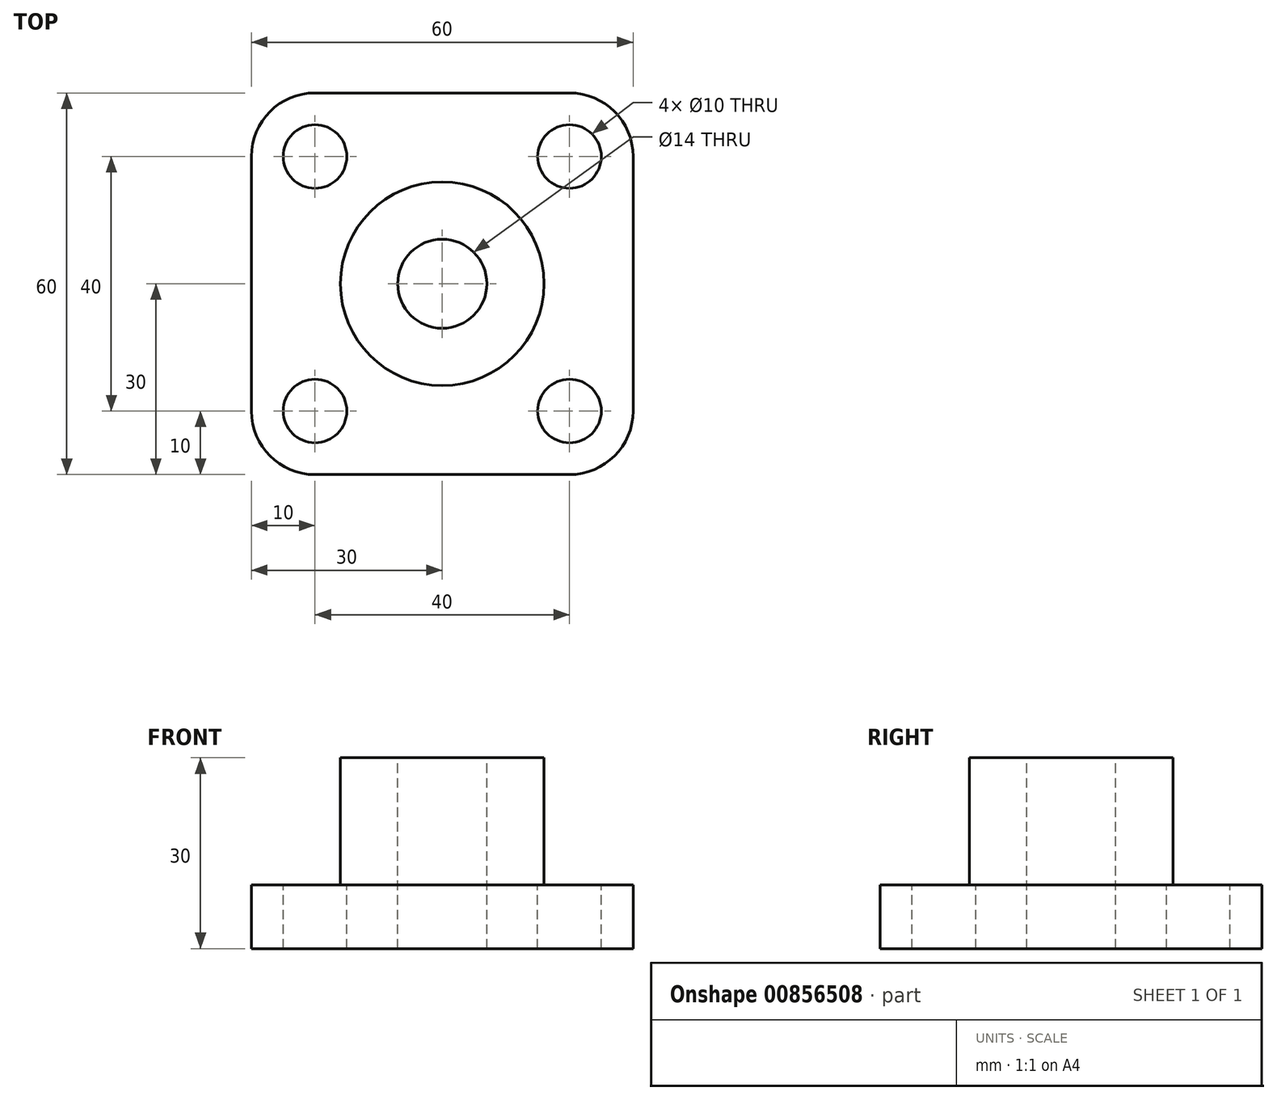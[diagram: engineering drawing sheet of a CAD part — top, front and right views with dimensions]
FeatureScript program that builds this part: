
annotation { "Feature Type Name" : "Feature", "Feature Type Description" : "" }
export const myFeature = defineFeature(function(context is Context, id is Id, definition is map)
    precondition{}
    {
        {
            var Q0;
            Q0=qCreatedBy(makeId("Top.planeOp"),FACE);
            var sketch = newSketch(context, id + "F0", { "sketchPlane" : qUnion([Q0])});
            skLineSegment(sketch, "E0.bottom", {"start": v(30, 30) * mm, "end": v(-30, 30) * mm});
            skLineSegment(sketch, "E0.top", {"start": v(30, -30) * mm, "end": v(-30, -30) * mm});
            skLineSegment(sketch, "E0.left", {"start": v(30, 30) * mm, "end": v(30, -30) * mm});
            skLineSegment(sketch, "E0.right", {"start": v(-30, 30) * mm, "end": v(-30, -30) * mm});
            skPoint(sketch, "E0.middle", {"position": v(0, 0) * mm});
            skSolve(sketch);
        }
        {
            var Q0;
            Q0=makeQuery(id+"F0.imprint","IMPRINT",FACE,{"disambiguationData":[TD([[makeQuery(id+"F0.imprint","IMPRINT",EDGE,{"derivedFrom":sQuery(id+"F0.wireOp",EDGE,"E0.bottom")}),1.0]])]});
            extrude(context, id + "F1", {"entities" : qUnion([Q0]), "depth" : 10 * mm, "offsetDistance" : 25 * mm});
        }
        {
            var Q0;
            Q0=makeQuery(id+"F1.opExtrude","SWEPT_EDGE",EDGE,{"disambiguationData":[OSD([sQuery(id+"F0.wireOp",EDGE,"E0.bottom"),sQuery(id+"F0.wireOp",EDGE,"E0.right")])]});
            var Q1;
            Q1=makeQuery(id+"F1.opExtrude","SWEPT_EDGE",EDGE,{"disambiguationData":[OSD([sQuery(id+"F0.wireOp",EDGE,"E0.top"),sQuery(id+"F0.wireOp",EDGE,"E0.right")])]});
            var Q2;
            Q2=makeQuery(id+"F1.opExtrude","SWEPT_EDGE",EDGE,{"disambiguationData":[OSD([sQuery(id+"F0.wireOp",EDGE,"E0.top"),sQuery(id+"F0.wireOp",EDGE,"E0.left")])]});
            var Q3;
            Q3=makeQuery(id+"F1.opExtrude","SWEPT_EDGE",EDGE,{"disambiguationData":[OSD([sQuery(id+"F0.wireOp",EDGE,"E0.bottom"),sQuery(id+"F0.wireOp",EDGE,"E0.left")])]});
            fillet(context, id + "F2", {"entities" : qUnion([Q0, Q1, Q2, Q3]), "radius" : 10 * mm, "tangentPropagation" : true, "allowEdgeOverflow" : false});
        }
        {
            var Q0;
            Q0=makeQuery(id+"F1.opExtrude","CAP_FACE",FACE,{"disambiguationData":[OSD([sQuery(id+"F0.wireOp",EDGE,"E0.bottom"),sQuery(id+"F0.wireOp",EDGE,"E0.top"),sQuery(id+"F0.wireOp",EDGE,"E0.left"),sQuery(id+"F0.wireOp",EDGE,"E0.right")])],"isStart":false});
            var sketch = newSketch(context, id + "F3", { "sketchPlane" : qUnion([Q0])});
            skCircle(sketch, "E1", {"center": v(0, 0) * mm, "radius": 16 * mm});
            skLineSegment(sketch, "E2", {"start": v(30, 0) * mm, "end": v(30, 3) * mm});
            skLineSegment(sketch, "E3", {"start": v(30, 3) * mm, "end": v(15.72, 3) * mm});
            skLineSegment(sketch, "E4", {"start": v(30, 0) * mm, "end": v(30, -3) * mm});
            skLineSegment(sketch, "E5", {"start": v(30, -3) * mm, "end": v(15.72, -3) * mm});
            skLineSegment(sketch, "E6", {"start": v(0, 30) * mm, "end": v(3, 30) * mm});
            skLineSegment(sketch, "E7", {"start": v(3, 30) * mm, "end": v(3, 15.72) * mm});
            skLineSegment(sketch, "E8", {"start": v(0, 30) * mm, "end": v(-3, 30) * mm});
            skLineSegment(sketch, "E9", {"start": v(-3, 30) * mm, "end": v(-3, 15.72) * mm});
            skLineSegment(sketch, "E10", {"start": v(-30, 0) * mm, "end": v(-30, 3) * mm});
            skLineSegment(sketch, "E11", {"start": v(-30, 3) * mm, "end": v(-15.72, 3) * mm});
            skLineSegment(sketch, "E12", {"start": v(-30, 0) * mm, "end": v(-30, -3) * mm});
            skLineSegment(sketch, "E13", {"start": v(-30, -3) * mm, "end": v(-15.72, -3) * mm});
            skLineSegment(sketch, "E14", {"start": v(0, -30) * mm, "end": v(3, -30) * mm});
            skLineSegment(sketch, "E15", {"start": v(3, -30) * mm, "end": v(3, -15.72) * mm});
            skLineSegment(sketch, "E16", {"start": v(0, -30) * mm, "end": v(-3, -30) * mm});
            skLineSegment(sketch, "E17", {"start": v(-3, -30) * mm, "end": v(-3, -15.72) * mm});
            skPoint(sketch, "E18", {"position": v(-20, 20) * mm});
            skPoint(sketch, "E19", {"position": v(20, 20) * mm});
            skPoint(sketch, "E20", {"position": v(20, -20) * mm});
            skPoint(sketch, "E21", {"position": v(-20, -20) * mm});
            skSolve(sketch);
        }
        {
            var Q0;
            {var subQ0=sQuery(id+"F3.wireOp",EDGE,"E1");var subQ5=makeQuery(id+"F3.imprint","INTERSECT",VERTEX,{"derivedFrom":[subQ0,sQuery(id+"F3.wireOp",EDGE,"E3")]});Q0=makeQuery(id+"F3.imprint","IMPRINT",FACE,{"disambiguationData":[TD([[makeQuery(id+"F3.imprint","IMPRINT",EDGE,{"disambiguationData":[TD([[subQ5,-1.0]])],"derivedFrom":subQ0}),1.0]])]});}
            extrude(context, id + "F4", {"entities" : qUnion([Q0]), "operationType" : NewBodyOperationType.ADD, "depth" : 20 * mm, "offsetDistance" : 25 * mm});
        }
        {
            var Q0;
            Q0=makeQuery(id+"F4.opExtrude","CAP_FACE",FACE,{"disambiguationData":[OSD([sQuery(id+"F3.wireOp",EDGE,"E1")])],"isStart":false});
            var sketch = newSketch(context, id + "F5", { "sketchPlane" : qUnion([Q0])});
            skPoint(sketch, "E22", {"position": v(0, 0) * mm});
            skSolve(sketch);
        }
        {
            var Q0;
            Q0=sQuery(id+"F5.wireOp",VERTEX,"E22");
            var Q1;
            Q1=makeQuery(id+"F1.opExtrude","SWEPT_BODY",BODY,{"disambiguationData":[OSD([sQuery(id+"F0.wireOp",EDGE,"E0.bottom"),sQuery(id+"F0.wireOp",EDGE,"E0.top"),sQuery(id+"F0.wireOp",EDGE,"E0.left"),sQuery(id+"F0.wireOp",EDGE,"E0.right")])]});
            hole(context, id + "F6", {"style" : HoleStyle.SIMPLE, "endStyle" : HoleEndStyle.THROUGH, "standardTappedOrClearance" : lookupTablePath({ "standard" : "ISO", "engagement" : "75%", "pitch" : "2 mm", "size" : "M16", "type" : "Tapped" }), "standardBlindInLast" : lookupTablePath({ "standard" : "ISO", "engagement" : "75%", "pitch" : "2 mm", "size" : "M16", "type" : "Tapped" }), "holeDiameter" : 14 * mm, "majorDiameter" : 16 * mm, "showTappedDepth" : true, "isTappedThrough" : true, "tappedDepth" : 25 * mm, "tapClearance" : 3, "startFromSketch" : true, "locations" : qUnion([Q0]), "scope" : qUnion([Q1])});
        }
        {
            var Q0;
            Q0=sQuery(id+"F3.wireOp",VERTEX,"E18");
            var Q1;
            Q1=sQuery(id+"F3.wireOp",VERTEX,"E21");
            var Q2;
            Q2=sQuery(id+"F3.wireOp",VERTEX,"E20");
            var Q3;
            Q3=sQuery(id+"F3.wireOp",VERTEX,"E19");
            var Q4;
            Q4=makeQuery(id+"F1.opExtrude","SWEPT_BODY",BODY,{"disambiguationData":[OSD([sQuery(id+"F0.wireOp",EDGE,"E0.bottom"),sQuery(id+"F0.wireOp",EDGE,"E0.top"),sQuery(id+"F0.wireOp",EDGE,"E0.left"),sQuery(id+"F0.wireOp",EDGE,"E0.right")])]});
            hole(context, id + "F7", {"style" : HoleStyle.SIMPLE, "endStyle" : HoleEndStyle.THROUGH, "holeDiameter" : 10 * mm, "majorDiameter" : 6.35 * mm, "isTappedThrough" : true, "tappedDepth" : 25 * mm, "tapClearance" : 3, "startFromSketch" : true, "locations" : qUnion([Q0, Q1, Q2, Q3]), "scope" : qUnion([Q4])});
        }
    });
